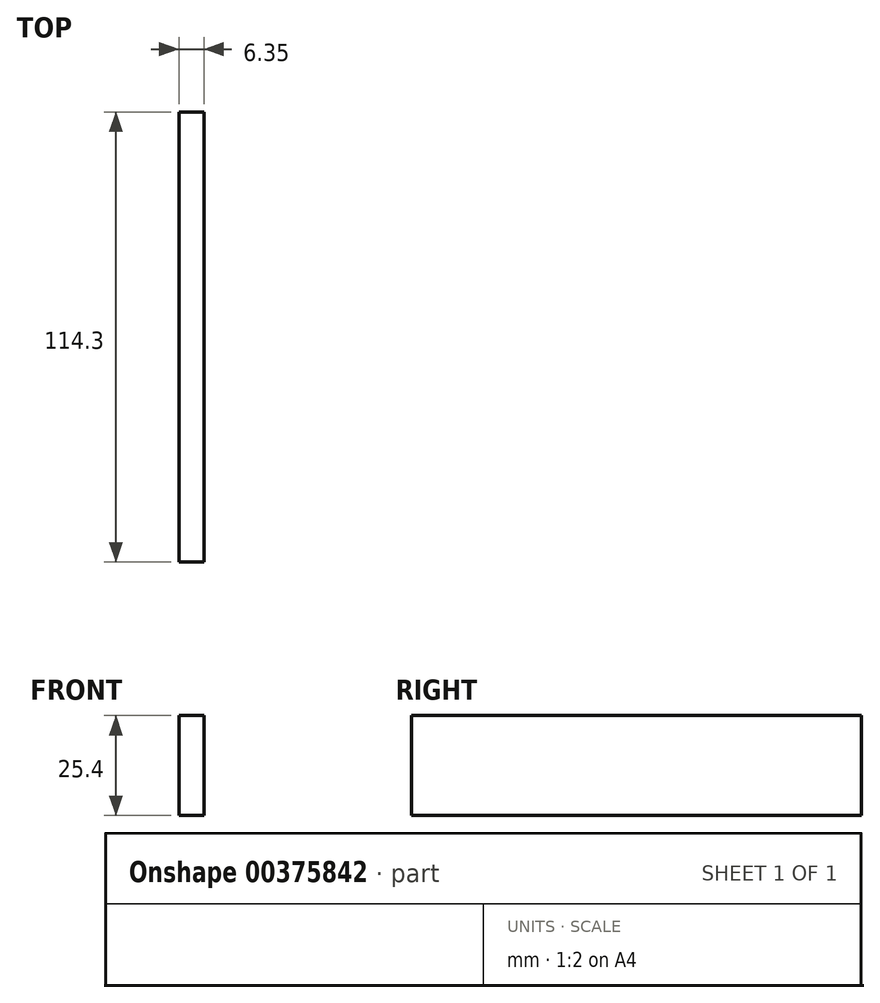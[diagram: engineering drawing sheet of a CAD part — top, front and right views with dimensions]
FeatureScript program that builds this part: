
annotation { "Feature Type Name" : "Feature", "Feature Type Description" : "" }
export const myFeature = defineFeature(function(context is Context, id is Id, definition is map)
    precondition{}
    {
        {
            var Q0;
            Q0=qCreatedBy(makeId("Right.planeOp"),FACE);
            var sketch = newSketch(context, id + "F0", { "sketchPlane" : qUnion([Q0])});
            skLineSegment(sketch, "E0.bottom", {"start": v(-87.66, -36.02) * mm, "end": v(26.64, -36.02) * mm});
            skLineSegment(sketch, "E0.top", {"start": v(-87.66, -61.42) * mm, "end": v(26.64, -61.42) * mm});
            skLineSegment(sketch, "E0.left", {"start": v(-87.66, -36.02) * mm, "end": v(-87.66, -61.42) * mm});
            skLineSegment(sketch, "E0.right", {"start": v(26.64, -36.02) * mm, "end": v(26.64, -61.42) * mm});
            skSolve(sketch);
        }
        {
            var Q0;
            Q0=qSketchRegion(id+"F0",true);
            extrude(context, id + "F1", {"entities" : qUnion([Q0]), "depth" : 6.35 * mm});
        }
    });
